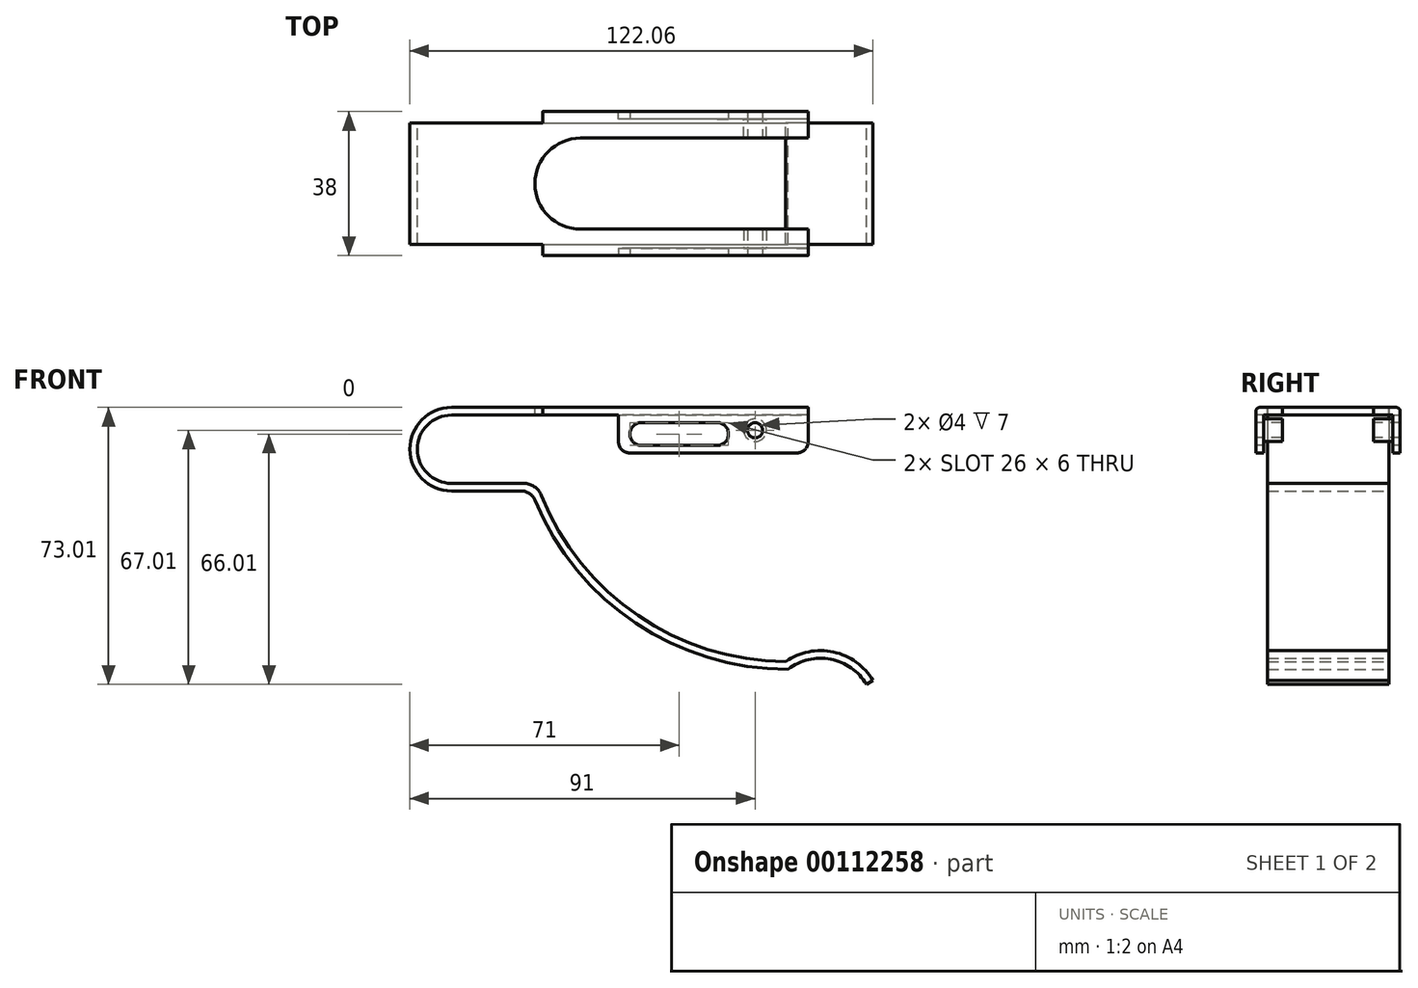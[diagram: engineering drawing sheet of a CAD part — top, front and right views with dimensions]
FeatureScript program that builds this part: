
annotation { "Feature Type Name" : "Feature", "Feature Type Description" : "" }
export const myFeature = defineFeature(function(context is Context, id is Id, definition is map)
    precondition{}
    {
        {
            var Q0;
            Q0=qCreatedBy(makeId("Front.planeOp"),FACE);
            var sketch = newSketch(context, id + "F0", { "sketchPlane" : qUnion([Q0])});
            skArc(sketch, "E0", {"start": v(0, 9) * mm, "mid": v(-9, 0) * mm, "end": v(0, -9) * mm});
            skLineSegment(sketch, "E1", {"start": v(0, 9) * mm, "end": v(94, 9) * mm});
            skLineSegment(sketch, "E2", {"start": v(0, -9) * mm, "end": v(19, -9) * mm});
            skArc(sketch, "E3", {"start": v(23.64, -12.13) * mm, "mid": v(49.18, -43.86) * mm, "end": v(88.07, -56) * mm});
            skArc(sketch, "E4", {"start": v(111.06, -61) * mm, "mid": v(100.66, -53.46) * mm, "end": v(88.07, -56) * mm});
            skPoint(sketch, "E5.visualSharp", {"position": v(22.46, -9) * mm});
            skArc(sketch, "E5.filletArc", {"start": v(23.64, -12.13) * mm, "mid": v(21.8, -9.86) * mm, "end": v(19, -9) * mm});
            skLineSegment(sketch, "E6.0", {"start": v(0, 11) * mm, "end": v(94, 11) * mm});
            skArc(sketch, "E6.1", {"start": v(109.34, -62.01) * mm, "mid": v(99.93, -55.35) * mm, "end": v(88.72, -58) * mm});
            skArc(sketch, "E6.2", {"start": v(22.03, -13.47) * mm, "mid": v(48.6, -45.88) * mm, "end": v(88.72, -58) * mm});
            skLineSegment(sketch, "E6.3", {"start": v(0, -11) * mm, "end": v(18.33, -11) * mm});
            skArc(sketch, "E6.4", {"start": v(0, 11) * mm, "mid": v(-11, 0) * mm, "end": v(0, -11) * mm});
            skLineSegment(sketch, "E7", {"start": v(94, 11) * mm, "end": v(94, 9) * mm});
            skLineSegment(sketch, "E8", {"start": v(111.06, -61) * mm, "end": v(109.34, -62.01) * mm});
            skPoint(sketch, "E9.visualSharp", {"position": v(21.06, -11) * mm});
            skArc(sketch, "E9.filletArc", {"start": v(22.03, -13.47) * mm, "mid": v(20.55, -11.68) * mm, "end": v(18.33, -11) * mm});
            skSolve(sketch);
        }
        {
            var Q0;
            Q0 = qSketchRegion(id + "F0", true);
            extrude(context, id + "F1", {"entities" : qUnion([Q0]), "depth" : 16 * mm});
        }
        {
            var Q0;
            Q0=makeQuery(id+"F1.opExtrude","SWEPT_FACE",FACE,{"disambiguationData":[OSD([sQuery(id+"F0.wireOp",EDGE,"E6.0")])]});
            var sketch = newSketch(context, id + "F2", { "sketchPlane" : qUnion([Q0])});
            skLineSegment(sketch, "E10.bottom", {"start": v(94, -16) * mm, "end": v(24, -16) * mm});
            skLineSegment(sketch, "E10.top", {"start": v(94, -19) * mm, "end": v(24, -19) * mm});
            skLineSegment(sketch, "E10.left", {"start": v(94, -16) * mm, "end": v(94, -19) * mm});
            skLineSegment(sketch, "E10.right", {"start": v(24, -16) * mm, "end": v(24, -19) * mm});
            skSolve(sketch);
        }
        {
            var Q0;
            Q0 = qSketchRegion(id + "F2", true);
            extrude(context, id + "F3", {"entities" : qUnion([Q0]), "operationType" : NewBodyOperationType.ADD, "oppositeDirection" : true, "depth" : 2 * mm});
        }
        {
            var Q0;
            Q0=makeQuery(id+"F3.opExtrude","SWEPT_FACE",FACE,{"disambiguationData":[OSD([sQuery(id+"F2.wireOp",EDGE,"E10.top")])]});
            var sketch = newSketch(context, id + "F4", { "sketchPlane" : qUnion([Q0])});
            skLineSegment(sketch, "E11.bottom", {"start": v(94, 9) * mm, "end": v(44, 9) * mm});
            skLineSegment(sketch, "E11.top", {"start": v(94, -1) * mm, "end": v(44, -1) * mm});
            skLineSegment(sketch, "E11.left", {"start": v(94, 9) * mm, "end": v(94, -1) * mm});
            skLineSegment(sketch, "E11.right", {"start": v(44, 9) * mm, "end": v(44, -1) * mm});
            skSolve(sketch);
        }
        {
            var Q0;
            Q0 = qSketchRegion(id + "F4", true);
            extrude(context, id + "F5", {"entities" : qUnion([Q0]), "operationType" : NewBodyOperationType.ADD, "oppositeDirection" : true, "depth" : 2 * mm});
        }
        {
            var Q0;
            Q0=makeQuery(id+"F3.opExtrude","CAP_EDGE",EDGE,{"disambiguationData":[OSD([sQuery(id+"F2.wireOp",EDGE,"E10.top")])],"isStart":true});
            fillet(context, id + "F6", {"entities" : qUnion([Q0]), "radius" : 1 * mm, "allowEdgeOverflow" : false});
        }
        {
            var Q0;
            Q0=makeQuery(id+"F1.opExtrude","SWEPT_BODY",BODY,{"disambiguationData":[OSD([sQuery(id+"F0.wireOp",EDGE,"E0"),sQuery(id+"F0.wireOp",EDGE,"E1"),sQuery(id+"F0.wireOp",EDGE,"E2"),sQuery(id+"F0.wireOp",EDGE,"E3"),sQuery(id+"F0.wireOp",EDGE,"E4"),sQuery(id+"F0.wireOp",EDGE,"E5.filletArc"),sQuery(id+"F0.wireOp",EDGE,"E6.0"),sQuery(id+"F0.wireOp",EDGE,"E6.1"),sQuery(id+"F0.wireOp",EDGE,"E6.2"),sQuery(id+"F0.wireOp",EDGE,"E6.3"),sQuery(id+"F0.wireOp",EDGE,"E6.4"),sQuery(id+"F0.wireOp",EDGE,"E7"),sQuery(id+"F0.wireOp",EDGE,"E8"),sQuery(id+"F0.wireOp",EDGE,"E9.filletArc")])]});
            var Q1;
            Q1=qCreatedBy(makeId("Front.planeOp"),FACE);
            mirror(context, id + "F7", {"operationType" : NewBodyOperationType.ADD, "entities" : qUnion([Q0]), "mirrorPlane" : qUnion([Q1])});
        }
        {
            var Q0;
            {var subQ0=makeQuery(id+"F3.boolean.opBoolean","MERGE",FACE,{"derivedFrom":[makeQuery(id+"F1.opExtrude","SWEPT_FACE",FACE,{"disambiguationData":[OSD([sQuery(id+"F0.wireOp",EDGE,"E6.0")])]}),makeQuery(id+"F3.opExtrude","CAP_FACE",FACE,{"disambiguationData":[OSD([sQuery(id+"F2.wireOp",EDGE,"E10.bottom"),sQuery(id+"F2.wireOp",EDGE,"E10.top"),sQuery(id+"F2.wireOp",EDGE,"E10.left"),sQuery(id+"F2.wireOp",EDGE,"E10.right")])],"isStart":true})]});Q0=makeQuery(id+"F7.boolean.opBoolean","MERGE",FACE,{"derivedFrom":[subQ0,makeQuery(id+"F7.opPattern","COPY",FACE,{"derivedFrom":subQ0,"instanceName":"1"})]});}
            var sketch = newSketch(context, id + "F8", { "sketchPlane" : qUnion([Q0])});
            skArc(sketch, "E12", {"start": v(34, 12) * mm, "mid": v(22, 0) * mm, "end": v(34, -12) * mm});
            skLineSegment(sketch, "E13", {"start": v(34, 12) * mm, "end": v(94, 12) * mm});
            skLineSegment(sketch, "E14", {"start": v(34, -12) * mm, "end": v(94, -12) * mm});
            skSolve(sketch);
        }
        {
            var Q0;
            Q0 = qSketchRegion(id + "F8", true);
            var Q1;
            Q1=makeQuery(id+"F8.imprint","IMPRINT",FACE,{"disambiguationData":[TD([[makeQuery(id+"F8.imprint","IMPRINT",EDGE,{"derivedFrom":sQuery(id+"F8.wireOp",EDGE,"E12")}),1.0]])]});
            extrude(context, id + "F9", {"entities" : qUnion([Q0, Q1]), "operationType" : NewBodyOperationType.REMOVE, "oppositeDirection" : true, "depth" : 10 * mm});
        }
        {
            var Q0;
            Q0=makeQuery(id+"F5.boolean.opBoolean","MERGE",FACE,{"derivedFrom":[makeQuery(id+"F3.opExtrude","SWEPT_FACE",FACE,{"disambiguationData":[OSD([sQuery(id+"F2.wireOp",EDGE,"E10.top")])]}),makeQuery(id+"F5.opExtrude","CAP_FACE",FACE,{"disambiguationData":[OSD([sQuery(id+"F4.wireOp",EDGE,"E11.bottom"),sQuery(id+"F4.wireOp",EDGE,"E11.top"),sQuery(id+"F4.wireOp",EDGE,"E11.left"),sQuery(id+"F4.wireOp",EDGE,"E11.right")])],"isStart":true})]});
            var sketch = newSketch(context, id + "F10", { "sketchPlane" : qUnion([Q0])});
            skLineSegment(sketch, "E15", {"start": v(50, 4) * mm, "end": v(70, 4) * mm});
            skArc(sketch, "E16.0.startCap", {"start": v(50, 1) * mm, "mid": v(47, 4) * mm, "end": v(50, 7) * mm});
            skArc(sketch, "E16.0.endCap", {"start": v(70, 7) * mm, "mid": v(73, 4) * mm, "end": v(70, 1) * mm});
            skLineSegment(sketch, "E16.0.left", {"start": v(50, 7) * mm, "end": v(70, 7) * mm});
            skLineSegment(sketch, "E16.0.right", {"start": v(50, 1) * mm, "end": v(70, 1) * mm});
            skSolve(sketch);
        }
        {
            var Q0;
            Q0 = qSketchRegion(id + "F10", true);
            extrude(context, id + "F11", {"entities" : qUnion([Q0]), "operationType" : NewBodyOperationType.REMOVE, "endBound" : BoundingType.THROUGH_ALL, "oppositeDirection" : true, "depth" : 25 * mm});
        }
        {
            var Q0;
            Q0=makeQuery(id+"F5.boolean.opBoolean","MERGE",FACE,{"derivedFrom":[makeQuery(id+"F3.opExtrude","SWEPT_FACE",FACE,{"disambiguationData":[OSD([sQuery(id+"F2.wireOp",EDGE,"E10.top")])]}),makeQuery(id+"F5.opExtrude","CAP_FACE",FACE,{"disambiguationData":[OSD([sQuery(id+"F4.wireOp",EDGE,"E11.bottom"),sQuery(id+"F4.wireOp",EDGE,"E11.top"),sQuery(id+"F4.wireOp",EDGE,"E11.left"),sQuery(id+"F4.wireOp",EDGE,"E11.right")])],"isStart":true})]});
            var sketch = newSketch(context, id + "F12", { "sketchPlane" : qUnion([Q0])});
            skPoint(sketch, "E17", {"position": v(80, 5) * mm});
            skSolve(sketch);
        }
        {
            var Q0;
            Q0=sQuery(id+"F12.wireOp",VERTEX,"E17");
            var Q1;
            Q1=makeQuery(id+"F1.opExtrude","SWEPT_BODY",BODY,{"disambiguationData":[OSD([sQuery(id+"F0.wireOp",EDGE,"E0"),sQuery(id+"F0.wireOp",EDGE,"E1"),sQuery(id+"F0.wireOp",EDGE,"E2"),sQuery(id+"F0.wireOp",EDGE,"E3"),sQuery(id+"F0.wireOp",EDGE,"E4"),sQuery(id+"F0.wireOp",EDGE,"E5.filletArc"),sQuery(id+"F0.wireOp",EDGE,"E6.0"),sQuery(id+"F0.wireOp",EDGE,"E6.1"),sQuery(id+"F0.wireOp",EDGE,"E6.2"),sQuery(id+"F0.wireOp",EDGE,"E6.3"),sQuery(id+"F0.wireOp",EDGE,"E6.4"),sQuery(id+"F0.wireOp",EDGE,"E7"),sQuery(id+"F0.wireOp",EDGE,"E8"),sQuery(id+"F0.wireOp",EDGE,"E9.filletArc")])]});
            hole(context, id + "F13", {"style" : HoleStyle.SIMPLE, "endStyle" : HoleEndStyle.THROUGH, "holeDiameter" : 4 * mm, "locations" : qUnion([Q0]), "scope" : qUnion([Q1]), "isTappedThrough" : true});
        }
        {
            var Q0;
            Q0=makeQuery(id+"F5.opExtrude","CAP_FACE",FACE,{"disambiguationData":[OSD([sQuery(id+"F4.wireOp",EDGE,"E11.bottom"),sQuery(id+"F4.wireOp",EDGE,"E11.top"),sQuery(id+"F4.wireOp",EDGE,"E11.left"),sQuery(id+"F4.wireOp",EDGE,"E11.right")])],"isStart":false});
            var sketch = newSketch(context, id + "F14", { "sketchPlane" : qUnion([Q0])});
            skCircle(sketch, "E18.0", {"center": v(-80, 5) * mm, "radius": 2 * mm});
            skCircle(sketch, "E19.0", {"center": v(-80, 5) * mm, "radius": 3 * mm});
            skSolve(sketch);
        }
        {
            var Q0;
            Q0 = qSketchRegion(id + "F14", true);
            extrude(context, id + "F15", {"entities" : qUnion([Q0]), "operationType" : NewBodyOperationType.ADD, "depth" : 5 * mm});
        }
        {
            var Q0;
            Q0=makeQuery(id+"F7.opPattern","COPY",FACE,{"derivedFrom":makeQuery(id+"F5.opExtrude","CAP_FACE",FACE,{"disambiguationData":[OSD([sQuery(id+"F4.wireOp",EDGE,"E11.bottom"),sQuery(id+"F4.wireOp",EDGE,"E11.top"),sQuery(id+"F4.wireOp",EDGE,"E11.left"),sQuery(id+"F4.wireOp",EDGE,"E11.right")])],"isStart":false}),"instanceName":"1"});
            var sketch = newSketch(context, id + "F16", { "sketchPlane" : qUnion([Q0])});
            skCircle(sketch, "E20.0", {"center": v(80, 5) * mm, "radius": 2 * mm});
            skCircle(sketch, "E21.0", {"center": v(80, 5) * mm, "radius": 3 * mm});
            skSolve(sketch);
        }
        {
            var Q0;
            Q0 = qSketchRegion(id + "F16", true);
            extrude(context, id + "F17", {"entities" : qUnion([Q0]), "operationType" : NewBodyOperationType.ADD, "depth" : 5 * mm});
        }
        {
            var Q0;
            Q0=makeQuery(id+"F5.opExtrude","SWEPT_EDGE",EDGE,{"disambiguationData":[OSD([sQuery(id+"F4.wireOp",EDGE,"E11.top"),sQuery(id+"F4.wireOp",EDGE,"E11.right")])]});
            var Q1;
            Q1=makeQuery(id+"F7.opPattern","COPY",EDGE,{"derivedFrom":makeQuery(id+"F5.opExtrude","SWEPT_EDGE",EDGE,{"disambiguationData":[OSD([sQuery(id+"F4.wireOp",EDGE,"E11.top"),sQuery(id+"F4.wireOp",EDGE,"E11.left")])]}),"instanceName":"1"});
            var Q2;
            Q2=makeQuery(id+"F5.opExtrude","SWEPT_EDGE",EDGE,{"disambiguationData":[OSD([sQuery(id+"F4.wireOp",EDGE,"E11.top"),sQuery(id+"F4.wireOp",EDGE,"E11.left")])]});
            var Q3;
            Q3=makeQuery(id+"F7.opPattern","COPY",EDGE,{"derivedFrom":makeQuery(id+"F5.opExtrude","SWEPT_EDGE",EDGE,{"disambiguationData":[OSD([sQuery(id+"F4.wireOp",EDGE,"E11.top"),sQuery(id+"F4.wireOp",EDGE,"E11.right")])]}),"instanceName":"1"});
            fillet(context, id + "F18", {"entities" : qUnion([Q0, Q1, Q2, Q3]), "radius" : 3 * mm, "tangentPropagation" : true, "allowEdgeOverflow" : false});
        }
    });
